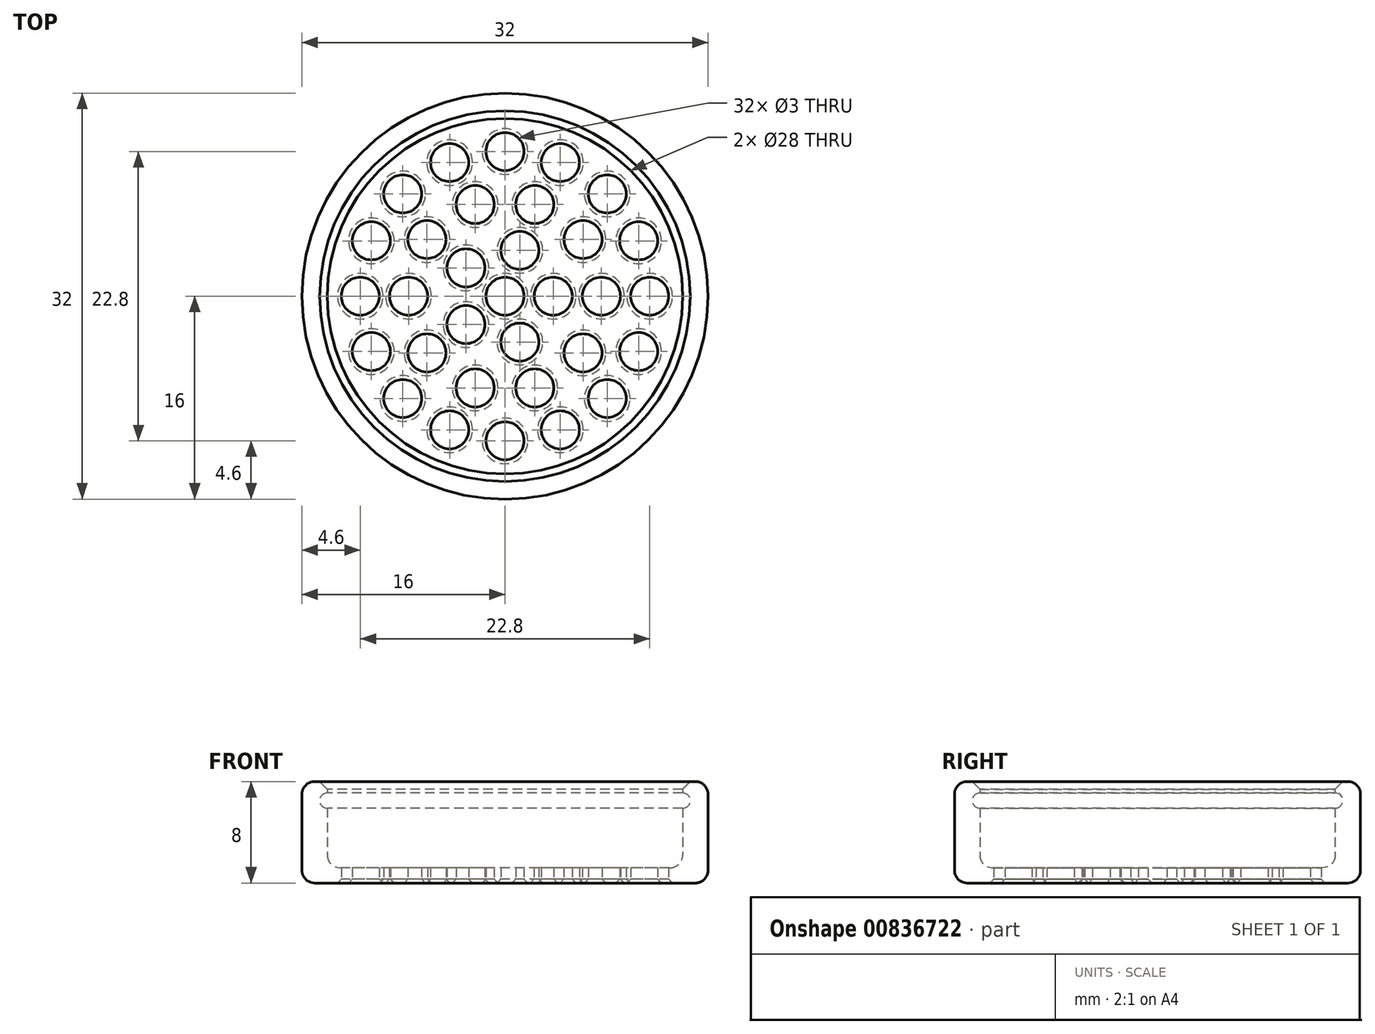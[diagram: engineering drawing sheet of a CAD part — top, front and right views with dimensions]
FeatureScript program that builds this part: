
annotation { "Feature Type Name" : "Feature", "Feature Type Description" : "" }
export const myFeature = defineFeature(function(context is Context, id is Id, definition is map)
    precondition{}
    {
        {
            var Q0;
            Q0=qCreatedBy(makeId("Top.planeOp"),FACE);
            var sketch = newSketch(context, id + "F0", { "sketchPlane" : qUnion([Q0])});
            skCircle(sketch, "E0", {"center": v(0, 0) * mm, "radius": 16 * mm});
            skCircle(sketch, "E1", {"center": v(0, 0) * mm, "radius": 14 * mm});
            skSolve(sketch);
        }
        {
            var Q0;
            Q0 = qSketchRegion(id + "F0", true);
            extrude(context, id + "F1", {"entities" : qUnion([Q0]), "depth" : 8 * mm, "offsetDistance" : 25 * mm});
        }
        {
            var Q0;
            Q0=qCreatedBy(makeId("Top.planeOp"),FACE);
            var sketch = newSketch(context, id + "F2", { "sketchPlane" : qUnion([Q0])});
            skCircle(sketch, "E2", {"center": v(0, 0) * mm, "radius": 1.5 * mm});
            skCircle(sketch, "E3.1.0.0", {"center": v(3.8, 0) * mm, "radius": 1.5 * mm});
            skCircle(sketch, "E3.2.0.0", {"center": v(7.6, 0) * mm, "radius": 1.5 * mm});
            skCircle(sketch, "E3.3.0.0", {"center": v(11.4, 0) * mm, "radius": 1.5 * mm});
            skLineSegment(sketch, "E3.direction1", {"start": v(0, 0) * mm, "end": v(3.8, 0) * mm, "construction": true});
            skCircle(sketch, "E4.1.0", {"center": v(10.53, 4.36) * mm, "radius": 1.5 * mm});
            skCircle(sketch, "E4.2.0", {"center": v(8.06, 8.06) * mm, "radius": 1.5 * mm});
            skCircle(sketch, "E4.3.0", {"center": v(4.36, 10.53) * mm, "radius": 1.5 * mm});
            skCircle(sketch, "E4.4.0", {"center": v(0, 11.4) * mm, "radius": 1.5 * mm});
            skCircle(sketch, "E4.5.0", {"center": v(-4.36, 10.53) * mm, "radius": 1.5 * mm});
            skCircle(sketch, "E4.6.0", {"center": v(-8.06, 8.06) * mm, "radius": 1.5 * mm});
            skCircle(sketch, "E4.7.0", {"center": v(-10.53, 4.36) * mm, "radius": 1.5 * mm});
            skCircle(sketch, "E4.8.0", {"center": v(-11.4, 0) * mm, "radius": 1.5 * mm});
            skCircle(sketch, "E4.9.0", {"center": v(-10.53, -4.36) * mm, "radius": 1.5 * mm});
            skCircle(sketch, "E4.10.0", {"center": v(-8.06, -8.06) * mm, "radius": 1.5 * mm});
            skCircle(sketch, "E4.11.0", {"center": v(-4.36, -10.53) * mm, "radius": 1.5 * mm});
            skCircle(sketch, "E4.12.0", {"center": v(0, -11.4) * mm, "radius": 1.5 * mm});
            skCircle(sketch, "E4.13.0", {"center": v(4.36, -10.53) * mm, "radius": 1.5 * mm});
            skCircle(sketch, "E4.14.0", {"center": v(8.06, -8.06) * mm, "radius": 1.5 * mm});
            skCircle(sketch, "E4.15.0", {"center": v(10.53, -4.36) * mm, "radius": 1.5 * mm});
            skCircle(sketch, "E5.1.0", {"center": v(6.15, 4.47) * mm, "radius": 1.5 * mm});
            skCircle(sketch, "E5.2.0", {"center": v(2.35, 7.23) * mm, "radius": 1.5 * mm});
            skCircle(sketch, "E5.3.0", {"center": v(-2.35, 7.23) * mm, "radius": 1.5 * mm});
            skCircle(sketch, "E5.4.0", {"center": v(-6.15, 4.47) * mm, "radius": 1.5 * mm});
            skCircle(sketch, "E5.5.0", {"center": v(-7.6, 0) * mm, "radius": 1.5 * mm});
            skCircle(sketch, "E5.6.0", {"center": v(-6.15, -4.47) * mm, "radius": 1.5 * mm});
            skCircle(sketch, "E5.7.0", {"center": v(-2.35, -7.23) * mm, "radius": 1.5 * mm});
            skCircle(sketch, "E5.8.0", {"center": v(2.35, -7.23) * mm, "radius": 1.5 * mm});
            skCircle(sketch, "E5.9.0", {"center": v(6.15, -4.47) * mm, "radius": 1.5 * mm});
            skCircle(sketch, "E6.1.0", {"center": v(1.17, 3.61) * mm, "radius": 1.5 * mm});
            skCircle(sketch, "E6.2.0", {"center": v(-3.07, 2.23) * mm, "radius": 1.5 * mm});
            skCircle(sketch, "E6.3.0", {"center": v(-3.07, -2.23) * mm, "radius": 1.5 * mm});
            skCircle(sketch, "E6.4.0", {"center": v(1.17, -3.61) * mm, "radius": 1.5 * mm});
            skCircle(sketch, "E7", {"center": v(0, 0) * mm, "radius": 15 * mm});
            skSolve(sketch);
        }
        {
            var Q0;
            Q0=makeQuery(id+"F2.imprint","IMPRINT",FACE,{"disambiguationData":[TD([[makeQuery(id+"F2.imprint","IMPRINT",EDGE,{"derivedFrom":sQuery(id+"F2.wireOp",EDGE,"E2")}),-1.0]])]});
            extrude(context, id + "F3", {"entities" : qUnion([Q0]), "depth" : 1.2 * mm, "offsetDistance" : 25 * mm});
        }
        {
            var Q0;
            Q0=makeQuery(id+"F1.opExtrude","SWEPT_BODY",BODY,{"disambiguationData":[OSD([sQuery(id+"F0.wireOp",EDGE,"E0"),sQuery(id+"F0.wireOp",EDGE,"E1")])]});
            var Q1;
            Q1=makeQuery(id+"F3.opExtrude","SWEPT_BODY",BODY,{"disambiguationData":[OSD([sQuery(id+"F2.wireOp",EDGE,"E2"),sQuery(id+"F2.wireOp",EDGE,"E3.1.0.0"),sQuery(id+"F2.wireOp",EDGE,"E3.2.0.0"),sQuery(id+"F2.wireOp",EDGE,"E3.3.0.0"),sQuery(id+"F2.wireOp",EDGE,"E4.1.0"),sQuery(id+"F2.wireOp",EDGE,"E4.2.0"),sQuery(id+"F2.wireOp",EDGE,"E4.3.0"),sQuery(id+"F2.wireOp",EDGE,"E4.4.0"),sQuery(id+"F2.wireOp",EDGE,"E4.5.0"),sQuery(id+"F2.wireOp",EDGE,"E4.6.0"),sQuery(id+"F2.wireOp",EDGE,"E4.7.0"),sQuery(id+"F2.wireOp",EDGE,"E4.8.0"),sQuery(id+"F2.wireOp",EDGE,"E4.9.0"),sQuery(id+"F2.wireOp",EDGE,"E4.10.0"),sQuery(id+"F2.wireOp",EDGE,"E4.11.0"),sQuery(id+"F2.wireOp",EDGE,"E4.12.0"),sQuery(id+"F2.wireOp",EDGE,"E4.13.0"),sQuery(id+"F2.wireOp",EDGE,"E4.14.0"),sQuery(id+"F2.wireOp",EDGE,"E4.15.0"),sQuery(id+"F2.wireOp",EDGE,"E5.1.0"),sQuery(id+"F2.wireOp",EDGE,"E5.2.0"),sQuery(id+"F2.wireOp",EDGE,"E5.3.0"),sQuery(id+"F2.wireOp",EDGE,"E5.4.0"),sQuery(id+"F2.wireOp",EDGE,"E5.5.0"),sQuery(id+"F2.wireOp",EDGE,"E5.6.0"),sQuery(id+"F2.wireOp",EDGE,"E5.7.0"),sQuery(id+"F2.wireOp",EDGE,"E5.8.0"),sQuery(id+"F2.wireOp",EDGE,"E5.9.0"),sQuery(id+"F2.wireOp",EDGE,"E6.1.0"),sQuery(id+"F2.wireOp",EDGE,"E6.2.0"),sQuery(id+"F2.wireOp",EDGE,"E6.3.0"),sQuery(id+"F2.wireOp",EDGE,"E6.4.0"),sQuery(id+"F2.wireOp",EDGE,"E7")])]});
            booleanBodies(context, id + "F4", {"operationType" : BooleanOperationType.UNION, "tools" : qUnion([Q0, Q1])});
        }
        {
            var Q0;
            Q0=qCreatedBy(makeId("Front.planeOp"),FACE);
            var sketch = newSketch(context, id + "F5", { "sketchPlane" : qUnion([Q0])});
            skLineSegment(sketch, "E8", {"start": v(-14, 5.9) * mm, "end": v(-14, 7.1) * mm});
            skArc(sketch, "E9", {"start": v(-14, 7.1) * mm, "mid": v(-14.6, 6.5) * mm, "end": v(-14, 5.9) * mm});
            skLineSegment(sketch, "E10", {"start": v(0, 0) * mm, "end": v(0, 9.72) * mm, "construction": true});
            skSolve(sketch);
        }
        {
            var Q0;
            Q0=makeQuery(id+"F5.imprint","IMPRINT",FACE,{"disambiguationData":[TD([[makeQuery(id+"F5.imprint","IMPRINT",EDGE,{"derivedFrom":sQuery(id+"F5.wireOp",EDGE,"E8")}),1.0]])]});
            var Q1;
            Q1=sQuery(id+"F5.wireOp",EDGE,"E10");
            revolve(context, id + "F6", {"operationType" : NewBodyOperationType.REMOVE, "surfaceOperationType" : NewSurfaceOperationType.NEW, "entities" : qUnion([Q0]), "axis" : qUnion([Q1]), "revolveType" : RevolveType.FULL, "oppositeDirection" : true});
        }
        {
            var Q0;
            Q0=makeQuery(id+"F1.opExtrude","CAP_EDGE",EDGE,{"disambiguationData":[OSD([sQuery(id+"F0.wireOp",EDGE,"E1")])],"isStart":false});
            chamfer(context, id + "F7", {"entities" : qUnion([Q0]), "width" : 0.6 * mm, "tangentPropagation" : true});
        }
        {
            var Q0;
            Q0=makeQuery(id+"F3.opExtrude","CAP_EDGE",EDGE,{"disambiguationData":[OSD([sQuery(id+"F2.wireOp",EDGE,"E4.9.0")])],"isStart":true});
            var Q1;
            Q1=makeQuery(id+"F3.opExtrude","CAP_EDGE",EDGE,{"disambiguationData":[OSD([sQuery(id+"F2.wireOp",EDGE,"E4.10.0")])],"isStart":true});
            var Q2;
            Q2=makeQuery(id+"F3.opExtrude","CAP_EDGE",EDGE,{"disambiguationData":[OSD([sQuery(id+"F2.wireOp",EDGE,"E4.11.0")])],"isStart":true});
            var Q3;
            Q3=makeQuery(id+"F3.opExtrude","CAP_EDGE",EDGE,{"disambiguationData":[OSD([sQuery(id+"F2.wireOp",EDGE,"E4.12.0")])],"isStart":true});
            var Q4;
            Q4=makeQuery(id+"F3.opExtrude","CAP_EDGE",EDGE,{"disambiguationData":[OSD([sQuery(id+"F2.wireOp",EDGE,"E4.13.0")])],"isStart":true});
            var Q5;
            Q5=makeQuery(id+"F3.opExtrude","CAP_EDGE",EDGE,{"disambiguationData":[OSD([sQuery(id+"F2.wireOp",EDGE,"E4.14.0")])],"isStart":true});
            var Q6;
            Q6=makeQuery(id+"F3.opExtrude","CAP_EDGE",EDGE,{"disambiguationData":[OSD([sQuery(id+"F2.wireOp",EDGE,"E4.15.0")])],"isStart":true});
            var Q7;
            Q7=makeQuery(id+"F3.opExtrude","CAP_EDGE",EDGE,{"disambiguationData":[OSD([sQuery(id+"F2.wireOp",EDGE,"E3.3.0.0")])],"isStart":true});
            var Q8;
            Q8=makeQuery(id+"F3.opExtrude","CAP_EDGE",EDGE,{"disambiguationData":[OSD([sQuery(id+"F2.wireOp",EDGE,"E4.1.0")])],"isStart":true});
            var Q9;
            Q9=makeQuery(id+"F3.opExtrude","CAP_EDGE",EDGE,{"disambiguationData":[OSD([sQuery(id+"F2.wireOp",EDGE,"E4.2.0")])],"isStart":true});
            var Q10;
            Q10=makeQuery(id+"F3.opExtrude","CAP_EDGE",EDGE,{"disambiguationData":[OSD([sQuery(id+"F2.wireOp",EDGE,"E4.3.0")])],"isStart":true});
            var Q11;
            Q11=makeQuery(id+"F3.opExtrude","CAP_EDGE",EDGE,{"disambiguationData":[OSD([sQuery(id+"F2.wireOp",EDGE,"E4.4.0")])],"isStart":true});
            var Q12;
            Q12=makeQuery(id+"F3.opExtrude","CAP_EDGE",EDGE,{"disambiguationData":[OSD([sQuery(id+"F2.wireOp",EDGE,"E4.5.0")])],"isStart":true});
            var Q13;
            Q13=makeQuery(id+"F3.opExtrude","CAP_EDGE",EDGE,{"disambiguationData":[OSD([sQuery(id+"F2.wireOp",EDGE,"E4.6.0")])],"isStart":true});
            var Q14;
            Q14=makeQuery(id+"F3.opExtrude","CAP_EDGE",EDGE,{"disambiguationData":[OSD([sQuery(id+"F2.wireOp",EDGE,"E4.7.0")])],"isStart":true});
            var Q15;
            Q15=makeQuery(id+"F3.opExtrude","CAP_EDGE",EDGE,{"disambiguationData":[OSD([sQuery(id+"F2.wireOp",EDGE,"E4.8.0")])],"isStart":true});
            var Q16;
            Q16=makeQuery(id+"F3.opExtrude","CAP_EDGE",EDGE,{"disambiguationData":[OSD([sQuery(id+"F2.wireOp",EDGE,"E5.5.0")])],"isStart":true});
            var Q17;
            Q17=makeQuery(id+"F3.opExtrude","CAP_EDGE",EDGE,{"disambiguationData":[OSD([sQuery(id+"F2.wireOp",EDGE,"E5.6.0")])],"isStart":true});
            var Q18;
            Q18=makeQuery(id+"F3.opExtrude","CAP_EDGE",EDGE,{"disambiguationData":[OSD([sQuery(id+"F2.wireOp",EDGE,"E5.7.0")])],"isStart":true});
            var Q19;
            Q19=makeQuery(id+"F3.opExtrude","CAP_EDGE",EDGE,{"disambiguationData":[OSD([sQuery(id+"F2.wireOp",EDGE,"E5.8.0")])],"isStart":true});
            var Q20;
            Q20=makeQuery(id+"F3.opExtrude","CAP_EDGE",EDGE,{"disambiguationData":[OSD([sQuery(id+"F2.wireOp",EDGE,"E5.9.0")])],"isStart":true});
            var Q21;
            Q21=makeQuery(id+"F3.opExtrude","CAP_EDGE",EDGE,{"disambiguationData":[OSD([sQuery(id+"F2.wireOp",EDGE,"E3.2.0.0")])],"isStart":true});
            var Q22;
            Q22=makeQuery(id+"F3.opExtrude","CAP_EDGE",EDGE,{"disambiguationData":[OSD([sQuery(id+"F2.wireOp",EDGE,"E5.1.0")])],"isStart":true});
            var Q23;
            Q23=makeQuery(id+"F3.opExtrude","CAP_EDGE",EDGE,{"disambiguationData":[OSD([sQuery(id+"F2.wireOp",EDGE,"E5.2.0")])],"isStart":true});
            var Q24;
            Q24=makeQuery(id+"F3.opExtrude","CAP_EDGE",EDGE,{"disambiguationData":[OSD([sQuery(id+"F2.wireOp",EDGE,"E5.3.0")])],"isStart":true});
            var Q25;
            Q25=makeQuery(id+"F3.opExtrude","CAP_EDGE",EDGE,{"disambiguationData":[OSD([sQuery(id+"F2.wireOp",EDGE,"E5.4.0")])],"isStart":true});
            var Q26;
            Q26=makeQuery(id+"F3.opExtrude","CAP_EDGE",EDGE,{"disambiguationData":[OSD([sQuery(id+"F2.wireOp",EDGE,"E6.2.0")])],"isStart":true});
            var Q27;
            Q27=makeQuery(id+"F3.opExtrude","CAP_EDGE",EDGE,{"disambiguationData":[OSD([sQuery(id+"F2.wireOp",EDGE,"E6.3.0")])],"isStart":true});
            var Q28;
            Q28=makeQuery(id+"F3.opExtrude","CAP_EDGE",EDGE,{"disambiguationData":[OSD([sQuery(id+"F2.wireOp",EDGE,"E2")])],"isStart":true});
            var Q29;
            Q29=makeQuery(id+"F3.opExtrude","CAP_EDGE",EDGE,{"disambiguationData":[OSD([sQuery(id+"F2.wireOp",EDGE,"E6.1.0")])],"isStart":true});
            var Q30;
            Q30=makeQuery(id+"F3.opExtrude","CAP_EDGE",EDGE,{"disambiguationData":[OSD([sQuery(id+"F2.wireOp",EDGE,"E6.4.0")])],"isStart":true});
            var Q31;
            Q31=makeQuery(id+"F3.opExtrude","CAP_EDGE",EDGE,{"disambiguationData":[OSD([sQuery(id+"F2.wireOp",EDGE,"E3.1.0.0")])],"isStart":true});
            chamfer(context, id + "F8", {"entities" : qUnion([Q0, Q1, Q2, Q3, Q4, Q5, Q6, Q7, Q8, Q9, Q10, Q11, Q12, Q13, Q14, Q15, Q16, Q17, Q18, Q19, Q20, Q21, Q22, Q23, Q24, Q25, Q26, Q27, Q28, Q29, Q30, Q31]), "width" : 0.3 * mm, "tangentPropagation" : true});
        }
        {
            var Q0;
            Q0=makeQuery(id+"F1.opExtrude","CAP_EDGE",EDGE,{"disambiguationData":[OSD([sQuery(id+"F0.wireOp",EDGE,"E0")])],"isStart":true});
            fillet(context, id + "F9", {"entities" : qUnion([Q0]), "radius" : 1 * mm, "tangentPropagation" : true, "allowEdgeOverflow" : false});
        }
        {
            var Q0;
            Q0=makeQuery(id+"F1.opExtrude","CAP_EDGE",EDGE,{"disambiguationData":[OSD([sQuery(id+"F0.wireOp",EDGE,"E0")])],"isStart":false});
            fillet(context, id + "F10", {"entities" : qUnion([Q0]), "radius" : 1 * mm, "tangentPropagation" : true, "allowEdgeOverflow" : false});
        }
        {
            var Q0;
            Q0=makeQuery(id+"F4.opBoolean","INTERSECT",EDGE,{"derivedFrom":[makeQuery(id+"F1.opExtrude","SWEPT_FACE",FACE,{"disambiguationData":[OSD([sQuery(id+"F0.wireOp",EDGE,"E1")])]}),makeQuery(id+"F3.opExtrude","CAP_FACE",FACE,{"disambiguationData":[OSD([sQuery(id+"F2.wireOp",EDGE,"E2"),sQuery(id+"F2.wireOp",EDGE,"E3.1.0.0"),sQuery(id+"F2.wireOp",EDGE,"E3.2.0.0"),sQuery(id+"F2.wireOp",EDGE,"E3.3.0.0"),sQuery(id+"F2.wireOp",EDGE,"E4.1.0"),sQuery(id+"F2.wireOp",EDGE,"E4.2.0"),sQuery(id+"F2.wireOp",EDGE,"E4.3.0"),sQuery(id+"F2.wireOp",EDGE,"E4.4.0"),sQuery(id+"F2.wireOp",EDGE,"E4.5.0"),sQuery(id+"F2.wireOp",EDGE,"E4.6.0"),sQuery(id+"F2.wireOp",EDGE,"E4.7.0"),sQuery(id+"F2.wireOp",EDGE,"E4.8.0"),sQuery(id+"F2.wireOp",EDGE,"E4.9.0"),sQuery(id+"F2.wireOp",EDGE,"E4.10.0"),sQuery(id+"F2.wireOp",EDGE,"E4.11.0"),sQuery(id+"F2.wireOp",EDGE,"E4.12.0"),sQuery(id+"F2.wireOp",EDGE,"E4.13.0"),sQuery(id+"F2.wireOp",EDGE,"E4.14.0"),sQuery(id+"F2.wireOp",EDGE,"E4.15.0"),sQuery(id+"F2.wireOp",EDGE,"E5.1.0"),sQuery(id+"F2.wireOp",EDGE,"E5.2.0"),sQuery(id+"F2.wireOp",EDGE,"E5.3.0"),sQuery(id+"F2.wireOp",EDGE,"E5.4.0"),sQuery(id+"F2.wireOp",EDGE,"E5.5.0"),sQuery(id+"F2.wireOp",EDGE,"E5.6.0"),sQuery(id+"F2.wireOp",EDGE,"E5.7.0"),sQuery(id+"F2.wireOp",EDGE,"E5.8.0"),sQuery(id+"F2.wireOp",EDGE,"E5.9.0"),sQuery(id+"F2.wireOp",EDGE,"E6.1.0"),sQuery(id+"F2.wireOp",EDGE,"E6.2.0"),sQuery(id+"F2.wireOp",EDGE,"E6.3.0"),sQuery(id+"F2.wireOp",EDGE,"E6.4.0"),sQuery(id+"F2.wireOp",EDGE,"E7")])],"isStart":false})]});
            fillet(context, id + "F11", {"entities" : qUnion([Q0]), "radius" : 1 * mm, "tangentPropagation" : true, "allowEdgeOverflow" : false});
        }
    });
